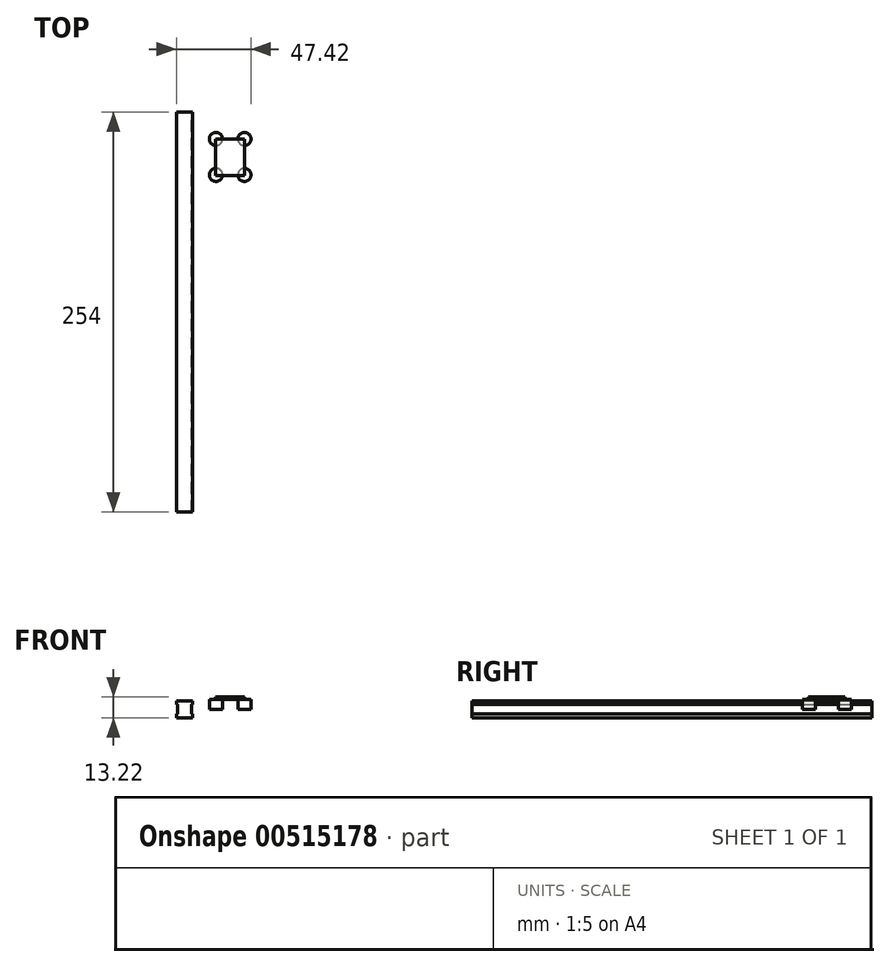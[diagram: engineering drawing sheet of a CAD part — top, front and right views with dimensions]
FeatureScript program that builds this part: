
annotation { "Feature Type Name" : "Feature", "Feature Type Description" : "" }
export const myFeature = defineFeature(function(context is Context, id is Id, definition is map)
    precondition{}
    {
        {
            var Q0;
            Q0=qCreatedBy(makeId("Front.planeOp"),FACE);
            var sketch = newSketch(context, id + "F0", { "sketchPlane" : qUnion([Q0])});
            skLineSegment(sketch, "E0.bottom", {"start": v(-6.22, 5.46) * mm, "end": v(4.14, 5.46) * mm});
            skLineSegment(sketch, "E0.top", {"start": v(-6.22, 3.07) * mm, "end": v(4.14, 3.07) * mm});
            skLineSegment(sketch, "E0.left", {"start": v(-6.22, 5.46) * mm, "end": v(-6.22, 3.07) * mm});
            skLineSegment(sketch, "E0.right", {"start": v(4.14, 5.46) * mm, "end": v(4.14, 3.07) * mm});
            skLineSegment(sketch, "E1.bottom", {"start": v(-6.22, -2.92) * mm, "end": v(4.14, -2.92) * mm});
            skLineSegment(sketch, "E1.top", {"start": v(-6.22, -5.32) * mm, "end": v(4.14, -5.32) * mm});
            skLineSegment(sketch, "E1.left", {"start": v(-6.22, -2.92) * mm, "end": v(-6.22, -5.32) * mm});
            skLineSegment(sketch, "E1.right", {"start": v(4.14, -2.92) * mm, "end": v(4.14, -5.32) * mm});
            skLineSegment(sketch, "E2.bottom", {"start": v(-5.5, 3.07) * mm, "end": v(3.42, 3.07) * mm});
            skLineSegment(sketch, "E2.top", {"start": v(-5.5, -2.92) * mm, "end": v(3.42, -2.92) * mm});
            skLineSegment(sketch, "E2.left", {"start": v(-5.5, 3.07) * mm, "end": v(-5.5, -2.92) * mm});
            skLineSegment(sketch, "E2.right", {"start": v(3.42, 3.07) * mm, "end": v(3.42, -2.92) * mm});
            skPoint(sketch, "E2.middle", {"position": v(-1.04, 0.07) * mm});
            skSolve(sketch);
        }
        {
            var Q0;
            Q0 = qSketchRegion(id + "F0", true);
            extrude(context, id + "F1", {"entities" : qUnion([Q0]), "depth" : 254 * mm, "offsetDistance" : 25.4 * mm});
        }
        {
            var Q0;
            Q0=qCreatedBy(makeId("Top.planeOp"),FACE);
            var sketch = newSketch(context, id + "F2", { "sketchPlane" : qUnion([Q0])});
            skCircle(sketch, "E3", {"center": v(18.9, -17.05) * mm, "radius": 4.18 * mm});
            skCircle(sketch, "E4", {"center": v(37.01, -17.05) * mm, "radius": 4.18 * mm});
            skCircle(sketch, "E5", {"center": v(37.01, -39.86) * mm, "radius": 4.18 * mm});
            skCircle(sketch, "E6", {"center": v(18.9, -39.86) * mm, "radius": 4.18 * mm});
            skSolve(sketch);
        }
        {
            var Q0;
            Q0 = qSketchRegion(id + "F2", true);
            extrude(context, id + "F3", {"entities" : qUnion([Q0]), "depth" : 6.35 * mm, "offsetDistance" : 25.4 * mm});
        }
        {
            var Q0;
            Q0=qCreatedBy(makeId("Top.planeOp"),FACE);
            var sketch = newSketch(context, id + "F4", { "sketchPlane" : qUnion([Q0])});
            skLineSegment(sketch, "E7.bottom", {"start": v(37.06, -40.22) * mm, "end": v(18.61, -40.22) * mm});
            skLineSegment(sketch, "E7.top", {"start": v(37.06, -16.98) * mm, "end": v(18.61, -16.98) * mm});
            skLineSegment(sketch, "E7.left", {"start": v(37.06, -40.22) * mm, "end": v(37.06, -16.98) * mm});
            skLineSegment(sketch, "E7.right", {"start": v(18.61, -40.22) * mm, "end": v(18.61, -16.98) * mm});
            skSolve(sketch);
        }
        {
            var Q0;
            Q0 = qSketchRegion(id + "F4", true);
            extrude(context, id + "F5", {"entities" : qUnion([Q0]), "depth" : 7.9 * mm, "offsetDistance" : 25.4 * mm, "hasSecondDirection" : true, "secondDirectionOppositeDirection" : false, "secondDirectionDepth" : 6.43 * mm});
        }
    });
